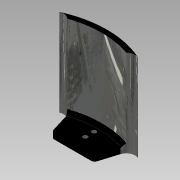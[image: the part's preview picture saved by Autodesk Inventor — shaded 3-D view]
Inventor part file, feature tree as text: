
AUTODESK INVENTOR PART (.ipt)
format: ipt  version: 2015 SP1 (Build 190203100, 203)  size: 164,864 bytes
history: native  units: mm
features: extrude x3, sketch x3, chamfer x1
ambient origin geometry x8: Origin, YZ Plane, XZ Plane, XY Plane, X Axis, Y Axis, Z Axis, Center Point
bodies: Solid1 (feature_tree)
feature tree (7):
  extrude  "Extrusion1"  Depth=5.0mm
  extrude  "Extrusion2"  Depth=1.291142mm
  extrude  "Extrusion3"  Depth=5.0mm
  chamfer  "Chamfer1"  Distance=20.705869mm
  sketch  "Sketch1"  dims[d0=5.0mm d1=2.0mm d2=2.5mm d3=2.5mm d4=34.377204mm]
  sketch  "Sketch2"  dims[d5=1.286842mm d6=1.291142mm]
  sketch  "Sketch3"  dims[d7=5.0mm d8=7.0mm d9=20.705869mm d10=10.020291mm d11=10.020291mm d12=13.361299mm d13=14.82011mm d14=53.698015mm d15=7.320812mm d16=3.0mm d17=0.0mm d18=3.5mm d19=46.0mm d20=0.0mm d21=3.0mm d22=1.907681mm d23=2.0mm d24=0.0mm d25=1.9mm d26=2.0mm d27=45.0deg]
